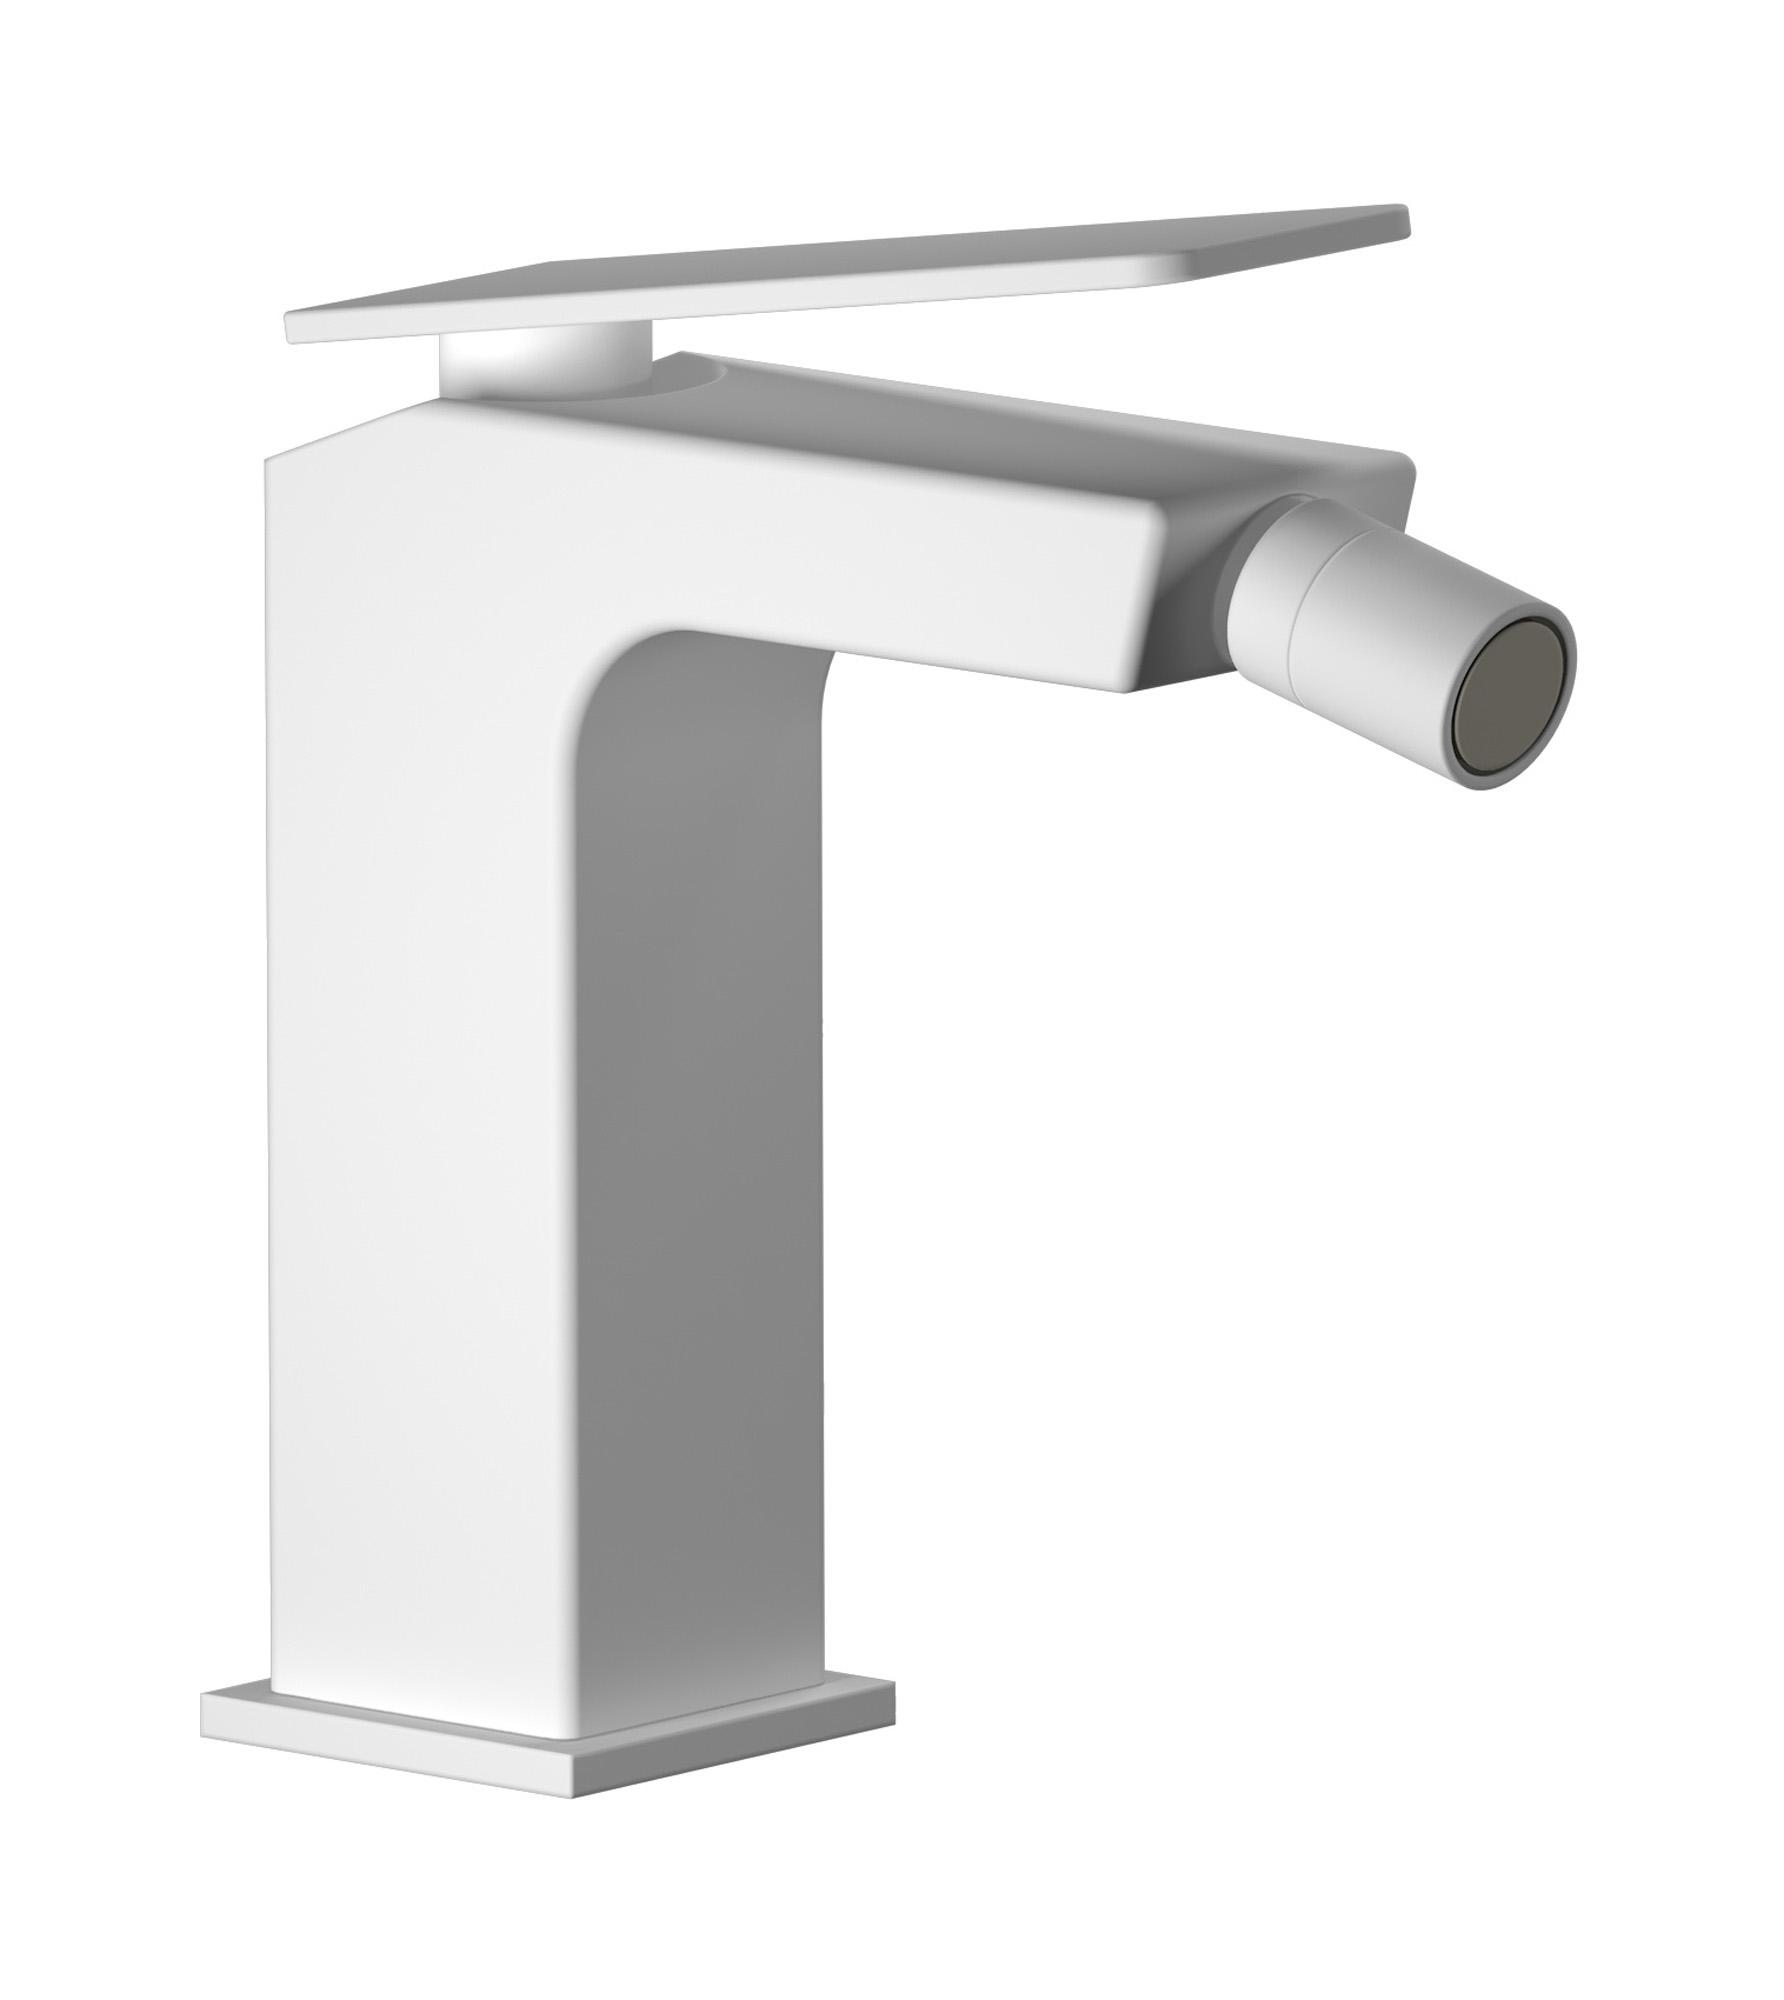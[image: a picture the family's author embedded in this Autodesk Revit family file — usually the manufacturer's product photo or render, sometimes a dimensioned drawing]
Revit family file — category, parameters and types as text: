
# Revit family: K3220
name_source: partatom
category: Apparecchi idraulici
units: mm (PartAtom-declared; Revit-internal decimal feet)

## family parameters
Basato su piano di lavoro = No
Condiviso = No
Mantieni orientamento annotazione = No
Numero OmniClass = 23.45.55.17
Punto di calcolo locali = No
Quota connettore circolare = Usa diametro
Sempre verticale = Sì
Taglio con vuoti quando caricato = No
Tipo di parte = Normale
Titolo OmniClass = Mixing Faucets

## types (8) — shared parameters
Cold water inlet = 10 mm  [stored 0.0328084 ft]
Commenti sul tipo = Bidet mixer
Connessione CW = No
Connessione HW = No
Connessione di scarico = No
Connessione di ventilazione = No
Descrizione = Monohole bidet mixer complete with drain
Hot water inlet = 10 mm  [stored 0.0328084 ft]
Produttore = IB Rubinetterie S.p.A.
URL = https://www.weareib.it
zero-valued in all types: Prospetto di default

## per-type parameters (varying)
| type | Finishes surface | Immagine tipo | Modello |
| Chrome | IB_Chrome | K3220CC.jpg | K3220CC |
| Brushed nickel | IB_Brushed nickel | K3220SS.jpg | K3220SS |
| Matt black | IB_matt black | K3220NP.jpg | K3220NP |
| Matt white | IB_matt white | K3220BO.jpg | K3220BO |
| Pale gold | IB_Pale gold | K3220II.jpg | K3220II |
| Brushed pale gold | IB_brushed pale gold | K3220IS.jpg | K3220IS |
| Rose gold | IB_Rose gold | K3220RS.jpg | K3220RS |
| Gold | IB_gold | K3220OO.jpg | K3220OO |

note: [stored X ft] marks values corroborated as IEEE doubles in the binary element streams (Revit-internal decimal feet)
